# Revit family: 10_MAGIS40-33_FN1A+STL
name_source: partatom
category: Finestre
units: mm (PartAtom-declared; Revit-internal decimal feet)

## family parameters
Condiviso = No
Host = Muro
Numero OmniClass = 23.30.20.00
Punto di calcolo locali = Sì
Sempre verticale = Sì
Taglio con vuoti quando caricato = No
Titolo OmniClass = Windows

## types (3) — shared parameters
Altezza di default del davanzale = 800 mm  [stored 2.62467 ft]
Chiusura muro = Per host
Costruzione analitica = <Nessuno>
EXTERNAL ALUMINUM FRAME/TELAIO ALLUMINIO ESTERNO = UNIFORM_ALUMINUM
GLASS WEIGHT/PESO VETRO = 30.00 kg/m²
HANDLE/MANIGLIA = UNIFORM_ALUMINUM
INTERIOR WOOD FRAME/TELAIO LEGNO INTERNO = UNIFORM_WOOD
Larghezza = 1000 mm  [stored 3.28084 ft]
MAXIMUM WIDTH/LARGHEZZA MASSIMA = 1200 mm  [stored 3.93701 ft]
MAX_DIMENSIONS_WARNING = No
MINIMUM WIDTH/LARGHEZZA MINIMA  = 400 mm  [stored 1.31234 ft]
Modello = MAGIS40
PRODUCER WEBSITE/SITO WEB PRODUTTORE = www.uniform.it
PRODUCT WEBSITE/SITO WEB PRODOTTO = www.sistema-uni-one.it
W = 1000 mm  [stored 3.28084 ft]
WINDOW GLASS/VETRO FINESTRA = UNIFORM_GLASS

## per-type parameters (varying)
| type | Altezza | FIXED WINDOW HEIGHT\ALTEZZA FINESTRA FISSA | H | HANDLE HEIGHT/ALTEZZA MANIGLIA | H_FIX | H_MOBILE | MAXIMUM HEIGHT/ALTEZZA MASSIMA | MINIMUM HEIGHT/ALTEZZA MINIMA | Rw GLASS/Rw VETRO | Rw WINDOW/Rw FINESTRA | Ug GLASS/Ug VETRO | Uw WINDOW/Uw FINESTRA |
| ACOUSTICS | 1500 mm  [stored 4.92126 ft] | 400 mm  [stored 1.31234 ft] | 1500 mm  [stored 4.92126 ft] | 600 mm | 400 mm  [stored 1.31234 ft] | 1100 mm | 2000 mm  [stored 6.56168 ft] | 400 mm  [stored 1.31234 ft] | 43 | 40 | 1.6 W/(m²·K) | 1.6 W/(m²·K) |
| THERMAL_PERFORMANCE | 1800 mm  [stored 5.90551 ft] | 1000 mm  [stored 3.28084 ft] | 1800 mm  [stored 5.90551 ft] | 500 mm  [stored 1.64042 ft] | 1000 mm  [stored 3.28084 ft] | 800 mm  [stored 2.62467 ft] | 2800 mm  [stored 9.18635 ft] | 800 mm  [stored 2.62467 ft] | 0 | 0 | 0.5 W/(m²·K) | 1.1 W/(m²·K) |
| THERMAL | 1800 mm  [stored 5.90551 ft] | 621 mm | 1800 mm  [stored 5.90551 ft] | 500 mm  [stored 1.64042 ft] | 621 mm | 1179 mm | 2800 mm  [stored 9.18635 ft] | 800 mm  [stored 2.62467 ft] | 0 | 0 | 1 W/(m²·K) | 1.4 W/(m²·K) |

note: [stored X ft] marks values corroborated as IEEE doubles in the binary element streams (Revit-internal decimal feet)
